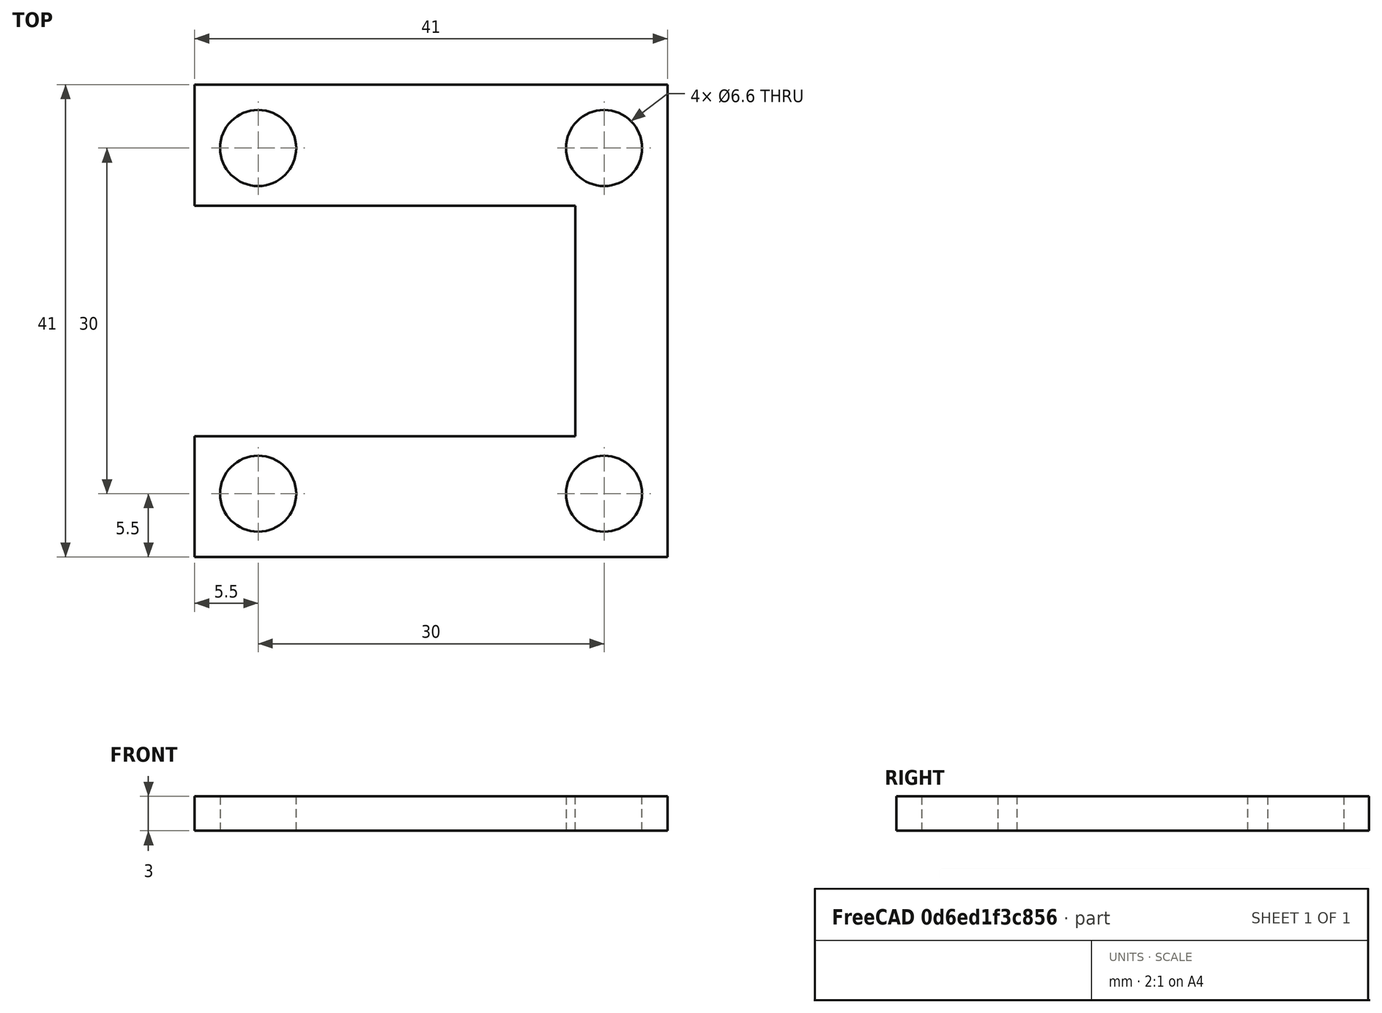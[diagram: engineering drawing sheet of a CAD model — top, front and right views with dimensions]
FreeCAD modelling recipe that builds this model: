
FCSTD DOCUMENT  (FreeCAD 0.16R6712 (Git))
Label: LCM calib3_3
License: All rights reserved
LicenseURL: http://en.wikipedia.org/wiki/All_rights_reserved
objects: Sketcher::SketchObject×1, PartDesign::Pad×1
note: 3 computed .brp shape members not serialized (recipe doc carries the construction recipe); baked Part::Feature solids carry a one-line shape summary decoded from their .brp

FEATURE [Sketcher::SketchObject] Sketch
  sketch-geometry (12):
    g0: LineSegment StartX=0 StartY=0 StartZ=0 EndX=41 EndY=0 EndZ=0
    g1: LineSegment StartX=41 StartY=0 StartZ=0 EndX=41 EndY=-41 EndZ=0
    g2: LineSegment StartX=41 StartY=-41 StartZ=0 EndX=0 EndY=-41 EndZ=0
    g3: LineSegment StartX=0 StartY=-41 StartZ=0 EndX=0 EndY=-30.5 EndZ=0
    g4: LineSegment StartX=0 StartY=-10.5 StartZ=0 EndX=33 EndY=-10.5 EndZ=0
    g5: LineSegment StartX=33 StartY=-10.5 StartZ=0 EndX=33 EndY=-30.5 EndZ=0
    g6: LineSegment StartX=33 StartY=-30.5 StartZ=0 EndX=0 EndY=-30.5 EndZ=0
    g7: Circle CenterX=5.5 CenterY=-5.5 CenterZ=0 NormalX=0 NormalY=0 NormalZ=1 Radius=3.3
    g8: Circle CenterX=35.5 CenterY=-5.5 CenterZ=0 NormalX=0 NormalY=0 NormalZ=1 Radius=3.3
    g9: Circle CenterX=5.5 CenterY=-35.5 CenterZ=0 NormalX=0 NormalY=0 NormalZ=1 Radius=3.3
    g10: Circle CenterX=35.5 CenterY=-35.5 CenterZ=0 NormalX=0 NormalY=0 NormalZ=1 Radius=3.3
    g11: LineSegment StartX=0 StartY=-10.5 StartZ=0 EndX=0 EndY=0 EndZ=0
  constraints (34):
    c: Coincident(g0,g1)
    c: Coincident(g1,g2)
    c: Coincident(g2,g3)
    c: Coincident(g11,g0)
    c: Horizontal(g0)
    c: Horizontal(g2)
    c: Vertical(g1)
    c: Vertical(g3)
    c: Coincident(g0,g-1)
    c: DistanceX(g0,g0) = 41
    c: DistanceY(g1,g1) = 41
    c: Coincident(g4,g5)
    c: Coincident(g5,g6)
    c: Horizontal(g4)
    c: Horizontal(g6)
    c: Vertical(g5)
    c: DistanceY(g5,g5) = 20
    c: DistanceX(g-1,g4) = 33
    c: Radius(g7) = 3.3
    c: Equal(g7,g9)
    c: Equal(g7,g8)
    c: Equal(g7,g10)
    c: DistanceY(g8,g7) = 0
    c: DistanceY(g10,g9) = 0
    c: DistanceX(g10,g8) = 0
    c: DistanceX(g9,g7) = 0
    c: DistanceX(g7,g8) = 30
    c: DistanceY(g10,g8) = 30
    c: DistanceX(g-1,g7) = 5.5
    c: DistanceY(g7,g-1) = 5.5
    c: Tangent(g3,g11)
    c: Coincident(g4,g11)
    c: Coincident(g6,g3)
    c: DistanceY(g4,g-1) = 10.5
FEATURE [PartDesign::Pad] Pad
  Length = 3
  Length2 = 100
  Sketch = -> Sketch
  Type = 0
